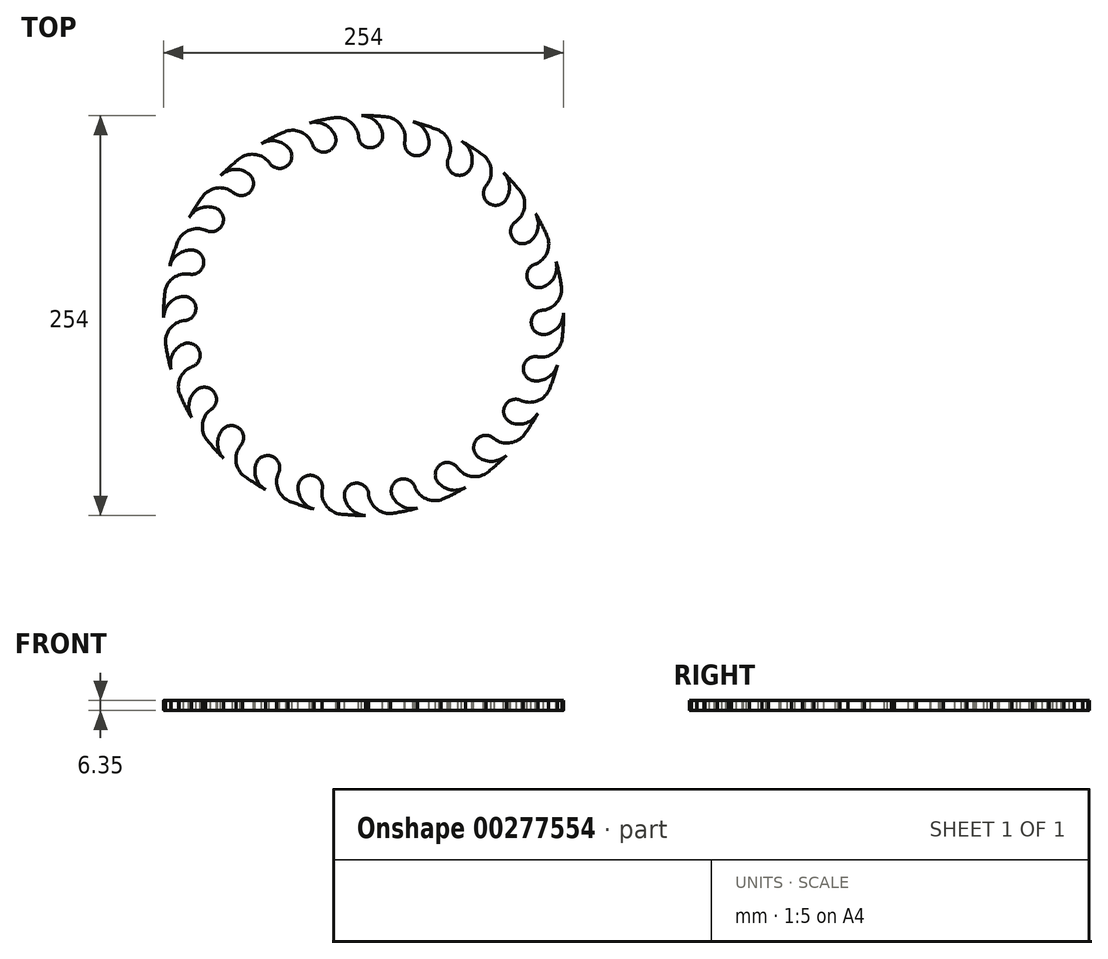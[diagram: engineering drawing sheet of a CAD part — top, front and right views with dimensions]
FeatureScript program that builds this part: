
annotation { "Feature Type Name" : "Feature", "Feature Type Description" : "" }
export const myFeature = defineFeature(function(context is Context, id is Id, definition is map)
    precondition{}
    {
        {
            var Q0;
            Q0=qCreatedBy(makeId("Top.planeOp"),FACE);
            var sketch = newSketch(context, id + "F0", { "sketchPlane" : qUnion([Q0])});
            skCircle(sketch, "E0", {"center": v(0, 0) * mm, "radius": 127 * mm});
            skSolve(sketch);
        }
        {
            var Q0;
            Q0=qSketchRegion(id+"F0",true);
            extrude(context, id + "F1", {"entities" : qUnion([Q0]), "depth" : 6.35 * mm});
        }
        {
            var Q0;
            Q0=makeQuery(id+"F1.opExtrude","CAP_FACE",FACE,{"disambiguationData":[OSD([sQuery(id+"F0.wireOp",EDGE,"E0")])],"isStart":false});
            var sketch = newSketch(context, id + "F2", { "sketchPlane" : qUnion([Q0])});
            skArc(sketch, "E1", {"start": v(54.26, 100.6) * mm, "mid": v(57.66, 89.7) * mm, "end": v(68.2, 94.08) * mm});
            skFitSpline(sketch, "E2", {"points": [v(53.43, 98.53) * mm, v(35.64, 121.12) * mm], "startDerivative": vector(39.71, 94.75) * mm, "endDerivative": vector(-18.42, -13.39) * mm});
            skArc(sketch, "E3", {"start": v(68.2, 94.08) * mm, "mid": v(68.07, 103.83) * mm, "end": v(61.55, 111.09) * mm});
            skArc(sketch, "E4", {"start": v(54.26, 100.6) * mm, "mid": v(54.32, 110.3) * mm, "end": v(47.95, 117.6) * mm});
            skArc(sketch, "E5.0", {"start": v(62.27, 110.68) * mm, "mid": v(55.22, 114.37) * mm, "end": v(47.95, 117.6) * mm});
            skArc(sketch, "E6.1.0", {"start": v(26.37, 111.2) * mm, "mid": v(32.48, 101.58) * mm, "end": v(41.52, 108.53) * mm});
            skArc(sketch, "E6.1.1", {"start": v(41.52, 108.53) * mm, "mid": v(38.87, 117.91) * mm, "end": v(30.7, 123.23) * mm});
            skArc(sketch, "E6.1.2", {"start": v(26.37, 111.2) * mm, "mid": v(23.92, 120.6) * mm, "end": v(15.87, 126) * mm});
            skArc(sketch, "E6.1.3", {"start": v(31.5, 123.03) * mm, "mid": v(23.74, 124.76) * mm, "end": v(15.87, 126) * mm});
            skArc(sketch, "E6.2.0", {"start": v(-3.3, 114.24) * mm, "mid": v(5.08, 106.52) * mm, "end": v(12.02, 115.58) * mm});
            skArc(sketch, "E6.2.1", {"start": v(12.02, 115.58) * mm, "mid": v(7.03, 123.96) * mm, "end": v(-2.24, 126.98) * mm});
            skArc(sketch, "E6.2.2", {"start": v(-3.3, 114.24) * mm, "mid": v(-8.1, 122.67) * mm, "end": v(-17.28, 125.82) * mm});
            skArc(sketch, "E6.2.3", {"start": v(-1.41, 127) * mm, "mid": v(-9.36, 126.65) * mm, "end": v(-17.28, 125.82) * mm});
            skArc(sketch, "E6.3.0", {"start": v(-32.76, 109.5) * mm, "mid": v(-22.66, 104.2) * mm, "end": v(-18.3, 114.75) * mm});
            skArc(sketch, "E6.3.1", {"start": v(-18.3, 114.75) * mm, "mid": v(-25.3, 121.55) * mm, "end": v(-35.03, 122.07) * mm});
            skArc(sketch, "E6.3.2", {"start": v(-32.76, 109.5) * mm, "mid": v(-39.58, 116.4) * mm, "end": v(-49.25, 117.06) * mm});
            skArc(sketch, "E6.3.3", {"start": v(-34.23, 122.3) * mm, "mid": v(-41.82, 119.92) * mm, "end": v(-49.25, 117.06) * mm});
            skArc(sketch, "E6.4.0", {"start": v(-59.99, 97.29) * mm, "mid": v(-48.86, 94.8) * mm, "end": v(-47.38, 106.1) * mm});
            skArc(sketch, "E6.4.1", {"start": v(-47.38, 106.1) * mm, "mid": v(-55.89, 110.87) * mm, "end": v(-65.43, 108.85) * mm});
            skArc(sketch, "E6.4.2", {"start": v(-59.99, 97.29) * mm, "mid": v(-68.36, 102.19) * mm, "end": v(-77.87, 100.32) * mm});
            skArc(sketch, "E6.4.3", {"start": v(-64.72, 109.27) * mm, "mid": v(-71.44, 105) * mm, "end": v(-77.87, 100.32) * mm});
            skArc(sketch, "E6.5.0", {"start": v(-83.12, 78.44) * mm, "mid": v(-71.73, 78.92) * mm, "end": v(-73.23, 90.22) * mm});
            skArc(sketch, "E6.5.1", {"start": v(-73.23, 90.22) * mm, "mid": v(-82.68, 92.62) * mm, "end": v(-91.37, 88.2) * mm});
            skArc(sketch, "E6.5.2", {"start": v(-83.12, 78.44) * mm, "mid": v(-92.47, 81.01) * mm, "end": v(-101.19, 76.75) * mm});
            skArc(sketch, "E6.5.3", {"start": v(-90.8, 88.8) * mm, "mid": v(-96.18, 82.94) * mm, "end": v(-101.19, 76.75) * mm});
            skArc(sketch, "E6.6.0", {"start": v(-100.6, 54.26) * mm, "mid": v(-89.7, 57.66) * mm, "end": v(-94.08, 68.2) * mm});
            skArc(sketch, "E6.6.1", {"start": v(-94.08, 68.2) * mm, "mid": v(-103.83, 68.07) * mm, "end": v(-111.09, 61.55) * mm});
            skArc(sketch, "E6.6.2", {"start": v(-100.6, 54.26) * mm, "mid": v(-110.3, 54.32) * mm, "end": v(-117.6, 47.95) * mm});
            skArc(sketch, "E6.6.3", {"start": v(-110.68, 62.27) * mm, "mid": v(-114.37, 55.22) * mm, "end": v(-117.6, 47.95) * mm});
            skArc(sketch, "E6.7.0", {"start": v(-111.2, 26.37) * mm, "mid": v(-101.58, 32.48) * mm, "end": v(-108.53, 41.52) * mm});
            skArc(sketch, "E6.7.1", {"start": v(-108.53, 41.52) * mm, "mid": v(-117.91, 38.87) * mm, "end": v(-123.23, 30.7) * mm});
            skArc(sketch, "E6.7.2", {"start": v(-111.2, 26.37) * mm, "mid": v(-120.6, 23.92) * mm, "end": v(-126, 15.87) * mm});
            skArc(sketch, "E6.7.3", {"start": v(-123.03, 31.5) * mm, "mid": v(-124.76, 23.74) * mm, "end": v(-126, 15.87) * mm});
            skArc(sketch, "E6.8.0", {"start": v(-114.24, -3.3) * mm, "mid": v(-106.52, 5.08) * mm, "end": v(-115.58, 12.02) * mm});
            skArc(sketch, "E6.8.1", {"start": v(-115.58, 12.02) * mm, "mid": v(-123.96, 7.03) * mm, "end": v(-126.98, -2.24) * mm});
            skArc(sketch, "E6.8.2", {"start": v(-114.24, -3.3) * mm, "mid": v(-122.67, -8.1) * mm, "end": v(-125.82, -17.28) * mm});
            skArc(sketch, "E6.8.3", {"start": v(-127, -1.41) * mm, "mid": v(-126.65, -9.36) * mm, "end": v(-125.82, -17.28) * mm});
            skArc(sketch, "E6.9.0", {"start": v(-109.5, -32.76) * mm, "mid": v(-104.2, -22.66) * mm, "end": v(-114.75, -18.3) * mm});
            skArc(sketch, "E6.9.1", {"start": v(-114.75, -18.3) * mm, "mid": v(-121.55, -25.3) * mm, "end": v(-122.07, -35.03) * mm});
            skArc(sketch, "E6.9.2", {"start": v(-109.5, -32.76) * mm, "mid": v(-116.4, -39.58) * mm, "end": v(-117.06, -49.25) * mm});
            skArc(sketch, "E6.9.3", {"start": v(-122.3, -34.23) * mm, "mid": v(-119.92, -41.82) * mm, "end": v(-117.06, -49.25) * mm});
            skArc(sketch, "E6.10.0", {"start": v(-97.29, -59.99) * mm, "mid": v(-94.8, -48.86) * mm, "end": v(-106.1, -47.38) * mm});
            skArc(sketch, "E6.10.1", {"start": v(-106.1, -47.38) * mm, "mid": v(-110.87, -55.89) * mm, "end": v(-108.85, -65.43) * mm});
            skArc(sketch, "E6.10.2", {"start": v(-97.29, -59.99) * mm, "mid": v(-102.19, -68.36) * mm, "end": v(-100.32, -77.87) * mm});
            skArc(sketch, "E6.10.3", {"start": v(-109.27, -64.72) * mm, "mid": v(-105, -71.44) * mm, "end": v(-100.32, -77.87) * mm});
            skArc(sketch, "E6.11.0", {"start": v(-78.44, -83.12) * mm, "mid": v(-78.92, -71.73) * mm, "end": v(-90.22, -73.23) * mm});
            skArc(sketch, "E6.11.1", {"start": v(-90.22, -73.23) * mm, "mid": v(-92.62, -82.68) * mm, "end": v(-88.2, -91.37) * mm});
            skArc(sketch, "E6.11.2", {"start": v(-78.44, -83.12) * mm, "mid": v(-81.01, -92.47) * mm, "end": v(-76.75, -101.19) * mm});
            skArc(sketch, "E6.11.3", {"start": v(-88.8, -90.8) * mm, "mid": v(-82.94, -96.18) * mm, "end": v(-76.75, -101.19) * mm});
            skArc(sketch, "E6.12.0", {"start": v(-54.26, -100.6) * mm, "mid": v(-57.66, -89.7) * mm, "end": v(-68.2, -94.08) * mm});
            skArc(sketch, "E6.12.1", {"start": v(-68.2, -94.08) * mm, "mid": v(-68.07, -103.83) * mm, "end": v(-61.55, -111.09) * mm});
            skArc(sketch, "E6.12.2", {"start": v(-54.26, -100.6) * mm, "mid": v(-54.32, -110.3) * mm, "end": v(-47.95, -117.6) * mm});
            skArc(sketch, "E6.12.3", {"start": v(-62.27, -110.68) * mm, "mid": v(-55.22, -114.37) * mm, "end": v(-47.95, -117.6) * mm});
            skArc(sketch, "E6.13.0", {"start": v(-26.37, -111.2) * mm, "mid": v(-32.48, -101.58) * mm, "end": v(-41.52, -108.53) * mm});
            skArc(sketch, "E6.13.1", {"start": v(-41.52, -108.53) * mm, "mid": v(-38.87, -117.91) * mm, "end": v(-30.7, -123.23) * mm});
            skArc(sketch, "E6.13.2", {"start": v(-26.37, -111.2) * mm, "mid": v(-23.92, -120.6) * mm, "end": v(-15.87, -126) * mm});
            skArc(sketch, "E6.13.3", {"start": v(-31.5, -123.03) * mm, "mid": v(-23.74, -124.76) * mm, "end": v(-15.87, -126) * mm});
            skArc(sketch, "E6.14.0", {"start": v(3.3, -114.24) * mm, "mid": v(-5.08, -106.52) * mm, "end": v(-12.02, -115.58) * mm});
            skArc(sketch, "E6.14.1", {"start": v(-12.02, -115.58) * mm, "mid": v(-7.03, -123.96) * mm, "end": v(2.24, -126.98) * mm});
            skArc(sketch, "E6.14.2", {"start": v(3.3, -114.24) * mm, "mid": v(8.1, -122.67) * mm, "end": v(17.28, -125.82) * mm});
            skArc(sketch, "E6.14.3", {"start": v(1.41, -127) * mm, "mid": v(9.36, -126.65) * mm, "end": v(17.28, -125.82) * mm});
            skArc(sketch, "E6.15.0", {"start": v(32.76, -109.5) * mm, "mid": v(22.66, -104.2) * mm, "end": v(18.3, -114.75) * mm});
            skArc(sketch, "E6.15.1", {"start": v(18.3, -114.75) * mm, "mid": v(25.3, -121.55) * mm, "end": v(35.03, -122.07) * mm});
            skArc(sketch, "E6.15.2", {"start": v(32.76, -109.5) * mm, "mid": v(39.58, -116.4) * mm, "end": v(49.25, -117.06) * mm});
            skArc(sketch, "E6.15.3", {"start": v(34.23, -122.3) * mm, "mid": v(41.82, -119.92) * mm, "end": v(49.25, -117.06) * mm});
            skArc(sketch, "E6.16.0", {"start": v(59.99, -97.29) * mm, "mid": v(48.86, -94.8) * mm, "end": v(47.38, -106.1) * mm});
            skArc(sketch, "E6.16.1", {"start": v(47.38, -106.1) * mm, "mid": v(55.89, -110.87) * mm, "end": v(65.43, -108.85) * mm});
            skArc(sketch, "E6.16.2", {"start": v(59.99, -97.29) * mm, "mid": v(68.36, -102.19) * mm, "end": v(77.87, -100.32) * mm});
            skArc(sketch, "E6.16.3", {"start": v(64.72, -109.27) * mm, "mid": v(71.44, -105) * mm, "end": v(77.87, -100.32) * mm});
            skArc(sketch, "E6.17.0", {"start": v(83.12, -78.44) * mm, "mid": v(71.73, -78.92) * mm, "end": v(73.23, -90.22) * mm});
            skArc(sketch, "E6.17.1", {"start": v(73.23, -90.22) * mm, "mid": v(82.68, -92.62) * mm, "end": v(91.37, -88.2) * mm});
            skArc(sketch, "E6.17.2", {"start": v(83.12, -78.44) * mm, "mid": v(92.47, -81.01) * mm, "end": v(101.19, -76.75) * mm});
            skArc(sketch, "E6.17.3", {"start": v(90.8, -88.8) * mm, "mid": v(96.18, -82.94) * mm, "end": v(101.19, -76.75) * mm});
            skArc(sketch, "E6.18.0", {"start": v(100.6, -54.26) * mm, "mid": v(89.7, -57.66) * mm, "end": v(94.08, -68.2) * mm});
            skArc(sketch, "E6.18.1", {"start": v(94.08, -68.2) * mm, "mid": v(103.83, -68.07) * mm, "end": v(111.09, -61.55) * mm});
            skArc(sketch, "E6.18.2", {"start": v(100.6, -54.26) * mm, "mid": v(110.3, -54.32) * mm, "end": v(117.6, -47.95) * mm});
            skArc(sketch, "E6.18.3", {"start": v(110.68, -62.27) * mm, "mid": v(114.37, -55.22) * mm, "end": v(117.6, -47.95) * mm});
            skArc(sketch, "E6.19.0", {"start": v(111.2, -26.37) * mm, "mid": v(101.58, -32.48) * mm, "end": v(108.53, -41.52) * mm});
            skArc(sketch, "E6.19.1", {"start": v(108.53, -41.52) * mm, "mid": v(117.91, -38.87) * mm, "end": v(123.23, -30.7) * mm});
            skArc(sketch, "E6.19.2", {"start": v(111.2, -26.37) * mm, "mid": v(120.6, -23.92) * mm, "end": v(126, -15.87) * mm});
            skArc(sketch, "E6.19.3", {"start": v(123.03, -31.5) * mm, "mid": v(124.76, -23.74) * mm, "end": v(126, -15.87) * mm});
            skArc(sketch, "E6.20.0", {"start": v(114.24, 3.3) * mm, "mid": v(106.52, -5.08) * mm, "end": v(115.58, -12.02) * mm});
            skArc(sketch, "E6.20.1", {"start": v(115.58, -12.02) * mm, "mid": v(123.96, -7.03) * mm, "end": v(126.98, 2.24) * mm});
            skArc(sketch, "E6.20.2", {"start": v(114.24, 3.3) * mm, "mid": v(122.67, 8.1) * mm, "end": v(125.82, 17.28) * mm});
            skArc(sketch, "E6.20.3", {"start": v(127, 1.41) * mm, "mid": v(126.65, 9.36) * mm, "end": v(125.82, 17.28) * mm});
            skArc(sketch, "E6.21.0", {"start": v(109.5, 32.76) * mm, "mid": v(104.2, 22.66) * mm, "end": v(114.75, 18.3) * mm});
            skArc(sketch, "E6.21.1", {"start": v(114.75, 18.3) * mm, "mid": v(121.55, 25.3) * mm, "end": v(122.07, 35.03) * mm});
            skArc(sketch, "E6.21.2", {"start": v(109.5, 32.76) * mm, "mid": v(116.4, 39.58) * mm, "end": v(117.06, 49.25) * mm});
            skArc(sketch, "E6.21.3", {"start": v(122.3, 34.23) * mm, "mid": v(119.92, 41.82) * mm, "end": v(117.06, 49.25) * mm});
            skArc(sketch, "E6.22.0", {"start": v(97.29, 59.99) * mm, "mid": v(94.8, 48.86) * mm, "end": v(106.1, 47.38) * mm});
            skArc(sketch, "E6.22.1", {"start": v(106.1, 47.38) * mm, "mid": v(110.87, 55.89) * mm, "end": v(108.85, 65.43) * mm});
            skArc(sketch, "E6.22.2", {"start": v(97.29, 59.99) * mm, "mid": v(102.19, 68.36) * mm, "end": v(100.32, 77.87) * mm});
            skArc(sketch, "E6.22.3", {"start": v(109.27, 64.72) * mm, "mid": v(105, 71.44) * mm, "end": v(100.32, 77.87) * mm});
            skArc(sketch, "E6.23.0", {"start": v(78.44, 83.12) * mm, "mid": v(78.92, 71.73) * mm, "end": v(90.22, 73.23) * mm});
            skArc(sketch, "E6.23.1", {"start": v(90.22, 73.23) * mm, "mid": v(92.62, 82.68) * mm, "end": v(88.2, 91.37) * mm});
            skArc(sketch, "E6.23.2", {"start": v(78.44, 83.12) * mm, "mid": v(81.01, 92.47) * mm, "end": v(76.75, 101.19) * mm});
            skArc(sketch, "E6.23.3", {"start": v(88.8, 90.8) * mm, "mid": v(82.94, 96.18) * mm, "end": v(76.75, 101.19) * mm});
            skSolve(sketch);
        }
        {
            var Q0;
            Q0 = qSketchRegion(id + "F2", true);
            extrude(context, id + "F3", {"entities" : qUnion([Q0]), "operationType" : NewBodyOperationType.REMOVE, "endBound" : BoundingType.THROUGH_ALL, "oppositeDirection" : true, "depth" : 25.4 * mm});
        }
    });
